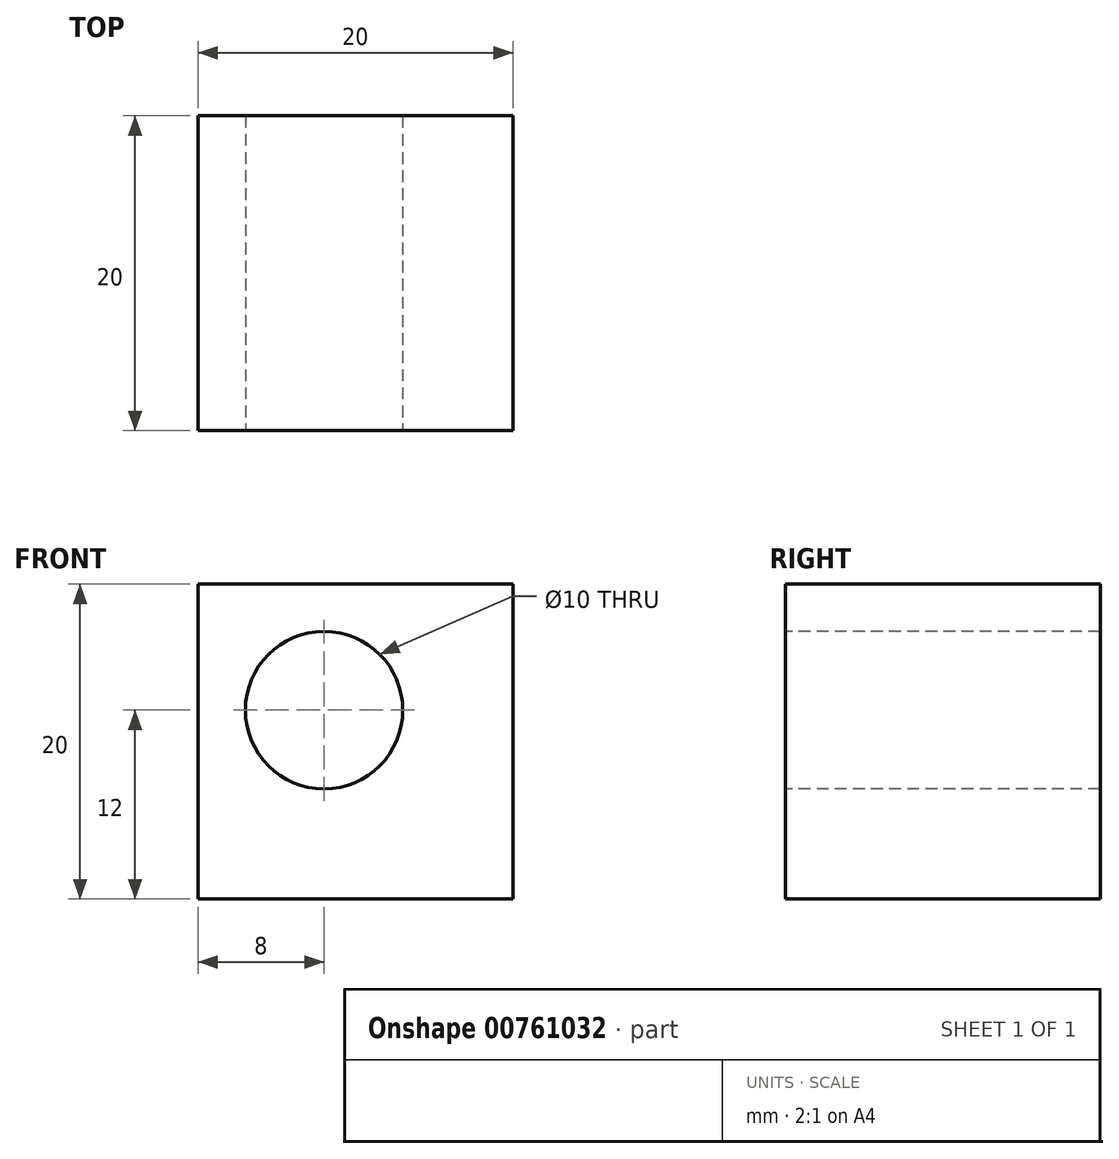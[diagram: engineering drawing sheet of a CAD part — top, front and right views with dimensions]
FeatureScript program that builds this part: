
annotation { "Feature Type Name" : "Feature", "Feature Type Description" : "" }
export const myFeature = defineFeature(function(context is Context, id is Id, definition is map)
    precondition{}
    {
        {
            var Q0;
            Q0=qCreatedBy(makeId("Front.planeOp"),FACE);
            var sketch = newSketch(context, id + "F0", { "sketchPlane" : qUnion([Q0])});
            skLineSegment(sketch, "E0.bottom", {"start": v(-10, 10) * mm, "end": v(10, 10) * mm});
            skLineSegment(sketch, "E0.top", {"start": v(-10, -10) * mm, "end": v(10, -10) * mm});
            skLineSegment(sketch, "E0.left", {"start": v(-10, 10) * mm, "end": v(-10, -10) * mm});
            skLineSegment(sketch, "E0.right", {"start": v(10, 10) * mm, "end": v(10, -10) * mm});
            skSolve(sketch);
        }
        {
            var Q0;
            Q0 = qSketchRegion(id + "F0", true);
            extrude(context, id + "F1", {"entities" : qUnion([Q0]), "endBound" : BoundingType.SYMMETRIC, "depth" : 20 * mm, "offsetDistance" : 25.4 * mm});
        }
        {
            var Q0;
            Q0=makeQuery(id+"F1.opExtrude","CAP_FACE",FACE,{"disambiguationData":[OSD([sQuery(id+"F0.wireOp",EDGE,"E0.bottom"),sQuery(id+"F0.wireOp",EDGE,"E0.top"),sQuery(id+"F0.wireOp",EDGE,"E0.left"),sQuery(id+"F0.wireOp",EDGE,"E0.right")])],"isStart":false});
            var sketch = newSketch(context, id + "F2", { "sketchPlane" : qUnion([Q0])});
            skCircle(sketch, "E1", {"center": v(-2, 2) * mm, "radius": 5 * mm});
            skSolve(sketch);
        }
        {
            var Q0;
            Q0 = qSketchRegion(id + "F2", true);
            extrude(context, id + "F3", {"entities" : qUnion([Q0]), "operationType" : NewBodyOperationType.REMOVE, "endBound" : BoundingType.THROUGH_ALL, "oppositeDirection" : true, "depth" : 37.5 * mm, "offsetDistance" : 25 * mm});
        }
    });
